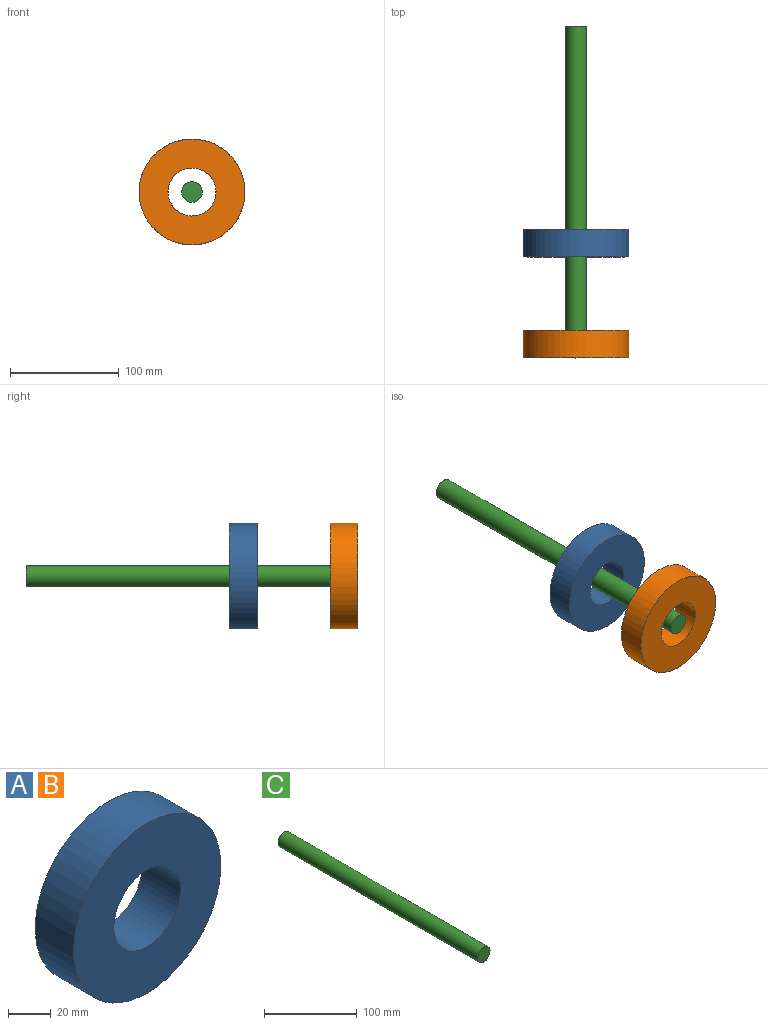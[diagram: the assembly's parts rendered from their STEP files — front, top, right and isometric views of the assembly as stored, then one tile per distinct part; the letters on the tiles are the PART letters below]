
ASSEMBLY  parts=3 mates=2
PART A: 4 faces, bbox 97.2x25.4x97.2 mm
  f0: cylinder r=22.07mm len=44.13mm, axis (0,1,0), area 3521.4mm2, adj f2,f3
  f1: cylinder r=48.58mm len=97.16mm, axis (0,1,0), area 7753.3mm2, adj f2,f3
  f2: plane 97.16x97.16mm, normal (0,-1,0), area 5885.2mm2, adj f0,f1
  f3: plane 97.16x97.16mm, normal (0,1,0), area 5885.2mm2, adj f0,f1
PART B: same geometry as A
PART C: 3 faces, bbox 19.1x304.8x19.1 mm
  f0: cylinder r=9.53mm len=304.8mm, axis (0,-1,0), area 18241.5mm2, adj f1,f2
  f1: plane 19.05x19.05mm, normal (0,1,0), area 285mm2, adj f0
  f2: plane 19.05x19.05mm, normal (0,-1,0), area 285mm2, adj f0
PLACE A rot(axis=(0,-1,0),25.1deg) t=(11.78,105.55,16.04)mm
PLACE B t=(11.78,12.85,16.04)mm
PLACE C t=(11.78,-12.55,16.04)mm fixed
MATE revolute B.f1 <-> C.f0  axis (0,-1,0) through (11.78,-12.55,16.04)mm
MATE cylindrical A.f0 <-> C.f0  axis (0,1,0) through (11.78,80.15,16.04)mm
